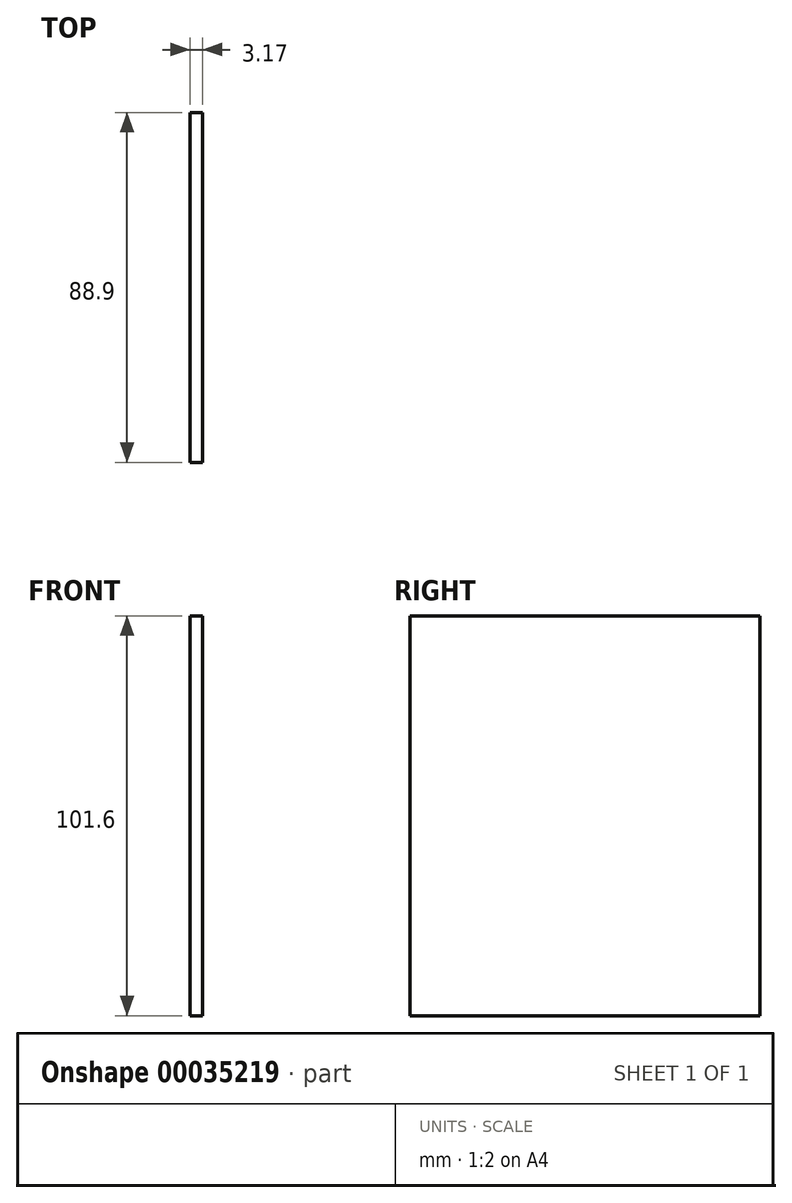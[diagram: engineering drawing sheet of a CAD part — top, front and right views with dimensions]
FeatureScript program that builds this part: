
annotation { "Feature Type Name" : "Feature", "Feature Type Description" : "" }
export const myFeature = defineFeature(function(context is Context, id is Id, definition is map)
    precondition{}
    {
        {
            var Q0;
            Q0=qCreatedBy(makeId("Right.planeOp"),FACE);
            var sketch = newSketch(context, id + "F0", { "sketchPlane" : qUnion([Q0])});
            skLineSegment(sketch, "E0.bottom", {"start": v(42.87, 43.96) * mm, "end": v(-46.03, 43.96) * mm});
            skLineSegment(sketch, "E0.top", {"start": v(42.87, -57.64) * mm, "end": v(-46.03, -57.64) * mm});
            skLineSegment(sketch, "E0.left", {"start": v(42.87, 43.96) * mm, "end": v(42.87, -57.64) * mm});
            skLineSegment(sketch, "E0.right", {"start": v(-46.03, 43.96) * mm, "end": v(-46.03, -57.64) * mm});
            skSolve(sketch);
        }
        {
            var Q0;
            Q0=makeQuery(id+"F0.imprint","IMPRINT",FACE,{"disambiguationData":[TD([[makeQuery(id+"F0.imprint","IMPRINT",EDGE,{"derivedFrom":sQuery(id+"F0.wireOp",EDGE,"E0.bottom")}),1.0]])]});
            extrude(context, id + "F1", {"entities" : qUnion([Q0]), "depth" : 3.17 * mm});
        }
    });
